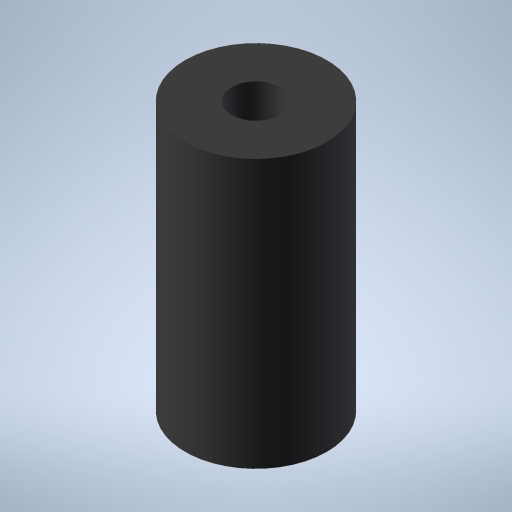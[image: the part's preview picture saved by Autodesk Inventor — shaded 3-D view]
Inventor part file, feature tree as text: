
AUTODESK INVENTOR PART (.ipt)
format: ipt  version: 2023 (Build 270158000, 158)  size: 516,096 bytes
history: native  units: in
note: dims shown in document units (in); Inventor stores cm internally (conversion verified against a paired STEP export)
features: extrude x2, sketch x2
ambient origin geometry x8: Origin, YZ Plane, XZ Plane, XY Plane, X Axis, Y Axis, Z Axis, Center Point
bodies: Solid1 (feature_tree)
feature tree (4):
  extrude  "Extrusion1"  Depth=0.4331in TaperAngle=0.0deg
  extrude  "Extrusion2"  Depth=0.4213in TaperAngle=0.0deg
  sketch  "Sketch1"  dims[d0=0.2283in d1=0.4331in d2=0.0in]
  sketch  "Sketch2"  dims[d3=0.0787in d4=0.4213in d5=0.0in]
